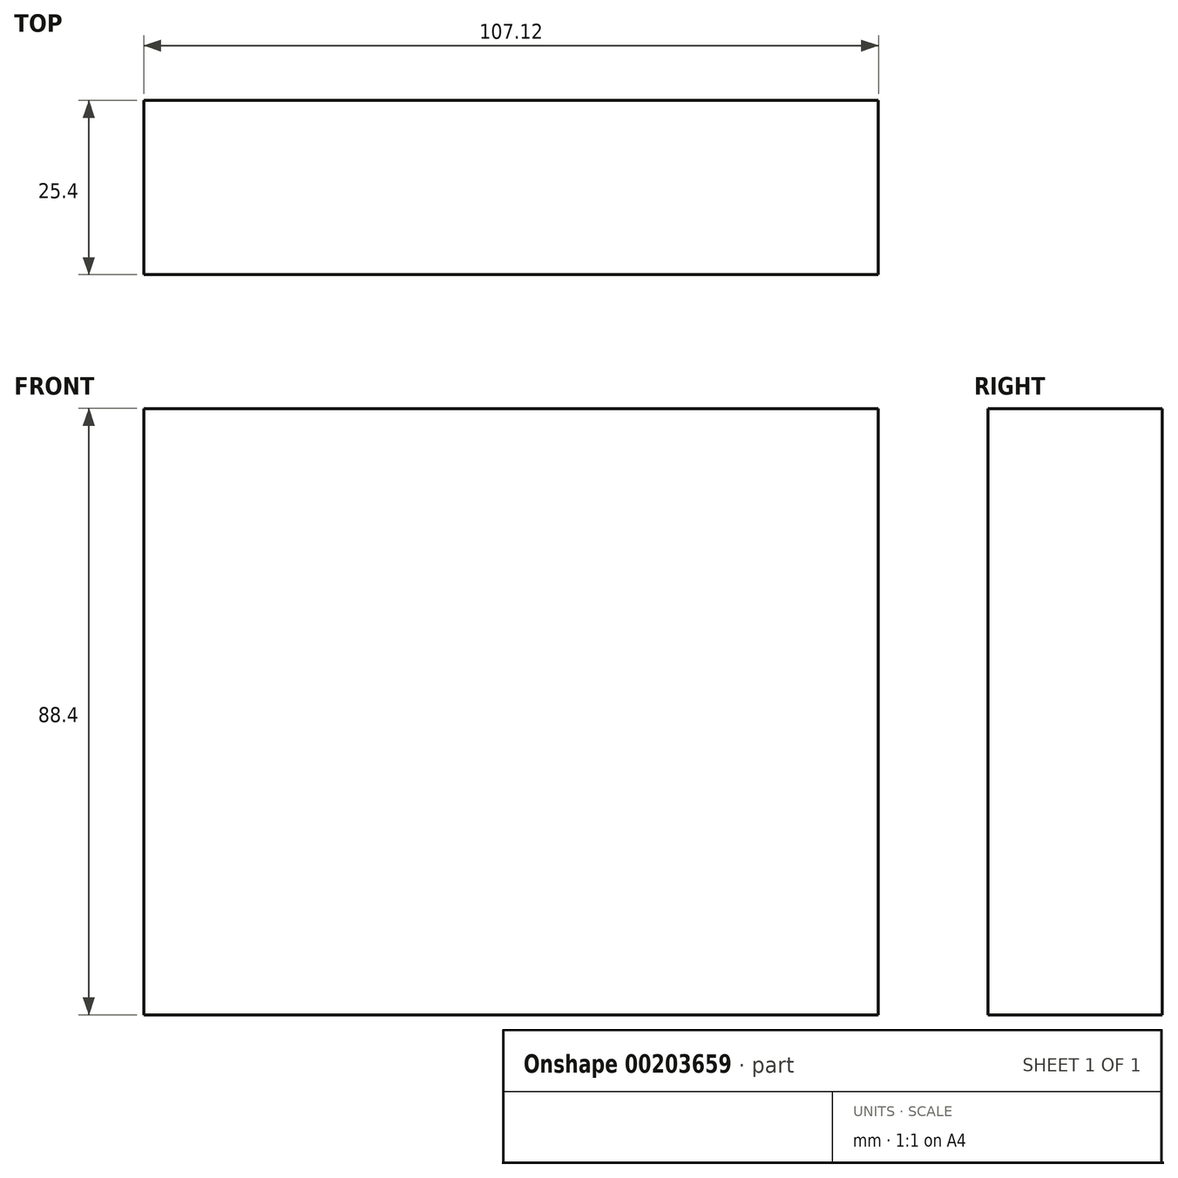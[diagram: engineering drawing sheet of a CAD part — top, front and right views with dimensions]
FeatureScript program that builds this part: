
annotation { "Feature Type Name" : "Feature", "Feature Type Description" : "" }
export const myFeature = defineFeature(function(context is Context, id is Id, definition is map)
    precondition{}
    {
        {
            var Q0;
            Q0=qCreatedBy(makeId("Front.planeOp"),FACE);
            var sketch = newSketch(context, id + "F3", { "sketchPlane" : qUnion([Q0])});
            skLineSegment(sketch, "E0.bottom", {"start": v(-53.56, 44.2) * mm, "end": v(53.56, 44.2) * mm});
            skLineSegment(sketch, "E0.top", {"start": v(-53.56, -44.2) * mm, "end": v(53.56, -44.2) * mm});
            skLineSegment(sketch, "E0.left", {"start": v(-53.56, 44.2) * mm, "end": v(-53.56, -44.2) * mm});
            skLineSegment(sketch, "E0.right", {"start": v(53.56, 44.2) * mm, "end": v(53.56, -44.2) * mm});
            skPoint(sketch, "E0.middle", {"position": v(0, 0) * mm});
            skSolve(sketch);
        }
        {
            var Q0;
            Q0 = qSketchRegion(id + "F3", true);
            extrude(context, id + "F0", {"entities" : qUnion([Q0]), "depth" : 25.4 * mm});
        }
    });
